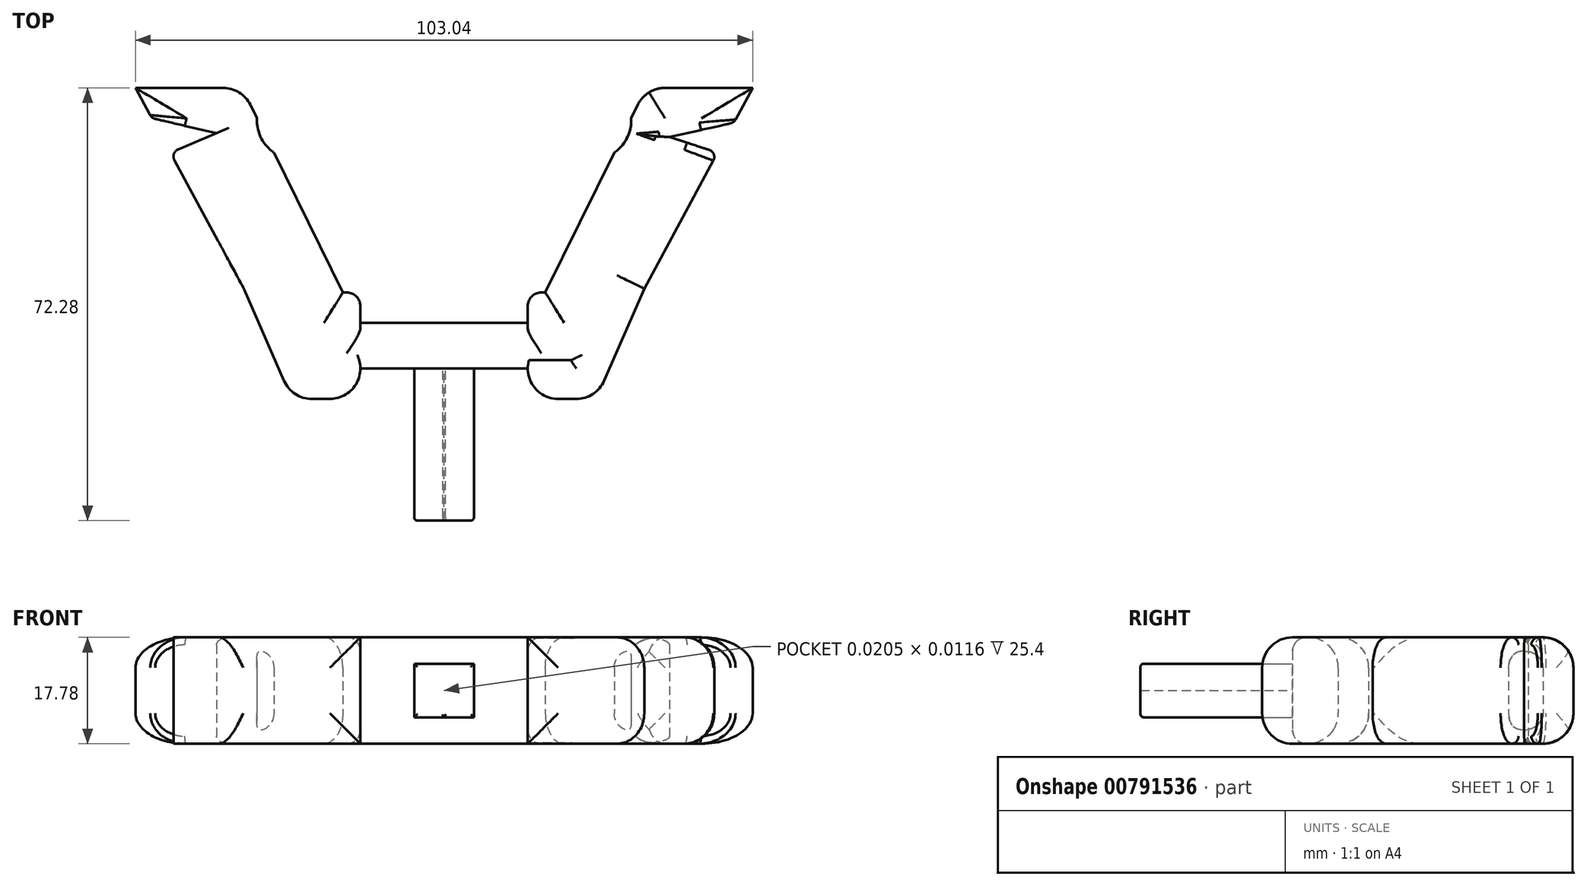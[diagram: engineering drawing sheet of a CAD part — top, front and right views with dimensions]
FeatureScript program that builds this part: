
annotation { "Feature Type Name" : "Feature", "Feature Type Description" : "" }
export const myFeature = defineFeature(function(context is Context, id is Id, definition is map)
    precondition{}
    {
        {
            var Q0;
            Q0=qCreatedBy(makeId("Top.planeOp"),FACE);
            var sketch = newSketch(context, id + "F0", { "sketchPlane" : qUnion([Q0])});
            skLineSegment(sketch, "E0", {"start": v(-38.82, 33.53) * mm, "end": v(-21.04, 33.53) * mm});
            skLineSegment(sketch, "E1", {"start": v(-38.82, 33.53) * mm, "end": v(-36.1, 28.48) * mm});
            skLineSegment(sketch, "E2", {"start": v(-21.04, 33.53) * mm, "end": v(-18.55, 28.48) * mm});
            skLineSegment(sketch, "E3", {"start": v(-4.2, -0.65) * mm, "end": v(-1.27, -0.65) * mm});
            skLineSegment(sketch, "E4", {"start": v(-20.73, 0) * mm, "end": v(-12.7, -18.43) * mm});
            skLineSegment(sketch, "E5", {"start": v(26.67, -0.65) * mm, "end": v(26.67, -5.73) * mm});
            skLineSegment(sketch, "E6", {"start": v(-12.7, -18.43) * mm, "end": v(-1.27, -18.43) * mm});
            skLineSegment(sketch, "E7", {"start": v(-16.66, 33.6) * mm, "end": v(-2.37, 4.57) * mm});
            skLineSegment(sketch, "E8", {"start": v(26.67, -18.43) * mm, "end": v(26.67, -13.35) * mm});
            skLineSegment(sketch, "E9.MirrorCS", {"start": v(42.06, 33.6) * mm, "end": v(27.77, 4.57) * mm});
            skLineSegment(sketch, "E10.MirrorCS", {"start": v(46.44, 33.53) * mm, "end": v(43.95, 28.48) * mm});
            skLineSegment(sketch, "E11.MirrorCS", {"start": v(29.6, -0.65) * mm, "end": v(26.67, -0.65) * mm});
            skLineSegment(sketch, "E12.MirrorCS", {"start": v(38.1, -18.43) * mm, "end": v(26.67, -18.43) * mm});
            skLineSegment(sketch, "E13.MirrorCS", {"start": v(46.13, 0) * mm, "end": v(38.1, -18.43) * mm});
            skLineSegment(sketch, "E14.MirrorCS", {"start": v(64.22, 33.53) * mm, "end": v(61.1, 27.74) * mm});
            skLineSegment(sketch, "E15.MirrorCS", {"start": v(64.22, 33.53) * mm, "end": v(46.44, 33.53) * mm});
            skLineSegment(sketch, "E16.trimOffspring", {"start": v(26.67, -5.73) * mm, "end": v(26.67, -0.65) * mm});
            skLineSegment(sketch, "E17.trimOffspring", {"start": v(26.67, -13.35) * mm, "end": v(26.67, -18.43) * mm});
            skLineSegment(sketch, "E18.trimOffspring", {"start": v(26.67, -5.73) * mm, "end": v(26.67, -1.8) * mm});
            skLineSegment(sketch, "E19", {"start": v(-1.27, -5.73) * mm, "end": v(-1.27, -0.65) * mm});
            skLineSegment(sketch, "E20", {"start": v(-1.27, -0.65) * mm, "end": v(-1.27, -5.73) * mm});
            skLineSegment(sketch, "E21.trimOffspring", {"start": v(-1.27, -13.35) * mm, "end": v(-1.27, -18.43) * mm});
            skArc(sketch, "E22", {"start": v(-18.55, 28.48) * mm, "mid": v(-17.88, 25.23) * mm, "end": v(-15.71, 22.72) * mm});
            skLineSegment(sketch, "E23.trimOffspring", {"start": v(-32.99, 22.72) * mm, "end": v(-20.73, 0) * mm});
            skLineSegment(sketch, "E24.trimOffspring", {"start": v(-15.71, 22.72) * mm, "end": v(-4.2, -0.65) * mm});
            skLineSegment(sketch, "E25", {"start": v(58.39, 22.72) * mm, "end": v(50.35, 25.32) * mm});
            skLineSegment(sketch, "E26", {"start": v(61.1, 27.74) * mm, "end": v(50.35, 25.32) * mm});
            skLineSegment(sketch, "E27.trimOffspring", {"start": v(58.39, 22.72) * mm, "end": v(46.13, 0) * mm});
            skLineSegment(sketch, "E28", {"start": v(-25.3, 25.97) * mm, "end": v(-36.1, 28.48) * mm});
            skLineSegment(sketch, "E29", {"start": v(-32.99, 22.72) * mm, "end": v(-25.3, 25.97) * mm});
            skLineSegment(sketch, "E30", {"start": v(-1.27, -5.73) * mm, "end": v(26.67, -5.73) * mm});
            skLineSegment(sketch, "E31", {"start": v(-1.27, -13.35) * mm, "end": v(26.67, -13.35) * mm});
            skArc(sketch, "E32", {"start": v(41.11, 22.72) * mm, "mid": v(43.28, 25.23) * mm, "end": v(43.95, 28.48) * mm});
            skLineSegment(sketch, "E33.trimOffspring", {"start": v(41.11, 22.72) * mm, "end": v(29.6, -0.65) * mm});
            skSolve(sketch);
        }
        {
            var Q0;
            Q0=makeQuery(id+"F0.imprint","IMPRINT",FACE,{"disambiguationData":[TD([[makeQuery(id+"F0.imprint","IMPRINT",EDGE,{"derivedFrom":sQuery(id+"F0.wireOp",EDGE,"E0")}),-1.0]])]});
            extrude(context, id + "F1", {"entities" : qUnion([Q0]), "depth" : 17.78 * mm, "offsetDistance" : 25.4 * mm});
        }
        {
            var Q0;
            Q0=makeQuery(id+"F1.opExtrude","CAP_EDGE",EDGE,{"disambiguationData":[OSD([sQuery(id+"F0.wireOp",EDGE,"E1")])],"isStart":false});
            var Q1;
            Q1=makeQuery(id+"F1.opExtrude","CAP_EDGE",EDGE,{"disambiguationData":[OSD([sQuery(id+"F0.wireOp",EDGE,"E2")])],"isStart":false});
            var Q2;
            Q2=makeQuery(id+"F1.opExtrude","CAP_EDGE",EDGE,{"disambiguationData":[OSD([sQuery(id+"F0.wireOp",EDGE,"E1")])],"isStart":true});
            var Q3;
            Q3=makeQuery(id+"F1.opExtrude","CAP_EDGE",EDGE,{"disambiguationData":[OSD([sQuery(id+"F0.wireOp",EDGE,"E2")])],"isStart":true});
            var Q4;
            Q4=makeQuery(id+"F1.opExtrude","SWEPT_FACE",FACE,{"disambiguationData":[OSD([sQuery(id+"F0.wireOp",EDGE,"E4")])]});
            var Q5;
            Q5=makeQuery(id+"F1.opExtrude","SWEPT_FACE",FACE,{"disambiguationData":[OSD([sQuery(id+"F0.wireOp",EDGE,"E6")])]});
            var Q6;
            Q6=makeQuery(id+"F1.opExtrude","CAP_EDGE",EDGE,{"disambiguationData":[OSD([sQuery(id+"F0.wireOp",EDGE,"E0")])],"isStart":false});
            var Q7;
            Q7=makeQuery(id+"F1.opExtrude","SWEPT_EDGE",EDGE,{"disambiguationData":[OSD([sQuery(id+"F0.wireOp",EDGE,"E0"),sQuery(id+"F0.wireOp",EDGE,"E2")])]});
            var Q8;
            Q8=makeQuery(id+"F1.opExtrude","CAP_EDGE",EDGE,{"disambiguationData":[OSD([sQuery(id+"F0.wireOp",EDGE,"E0")])],"isStart":true});
            fillet(context, id + "F2", {"entities" : qUnion([Q0, Q1, Q2, Q3, Q4, Q5, Q6, Q7, Q8]), "radius" : 5.08 * mm, "tangentPropagation" : true, "allowEdgeOverflow" : false});
        }
        {
            var Q0;
            Q0=makeQuery(id+"F1.opExtrude","CAP_EDGE",EDGE,{"disambiguationData":[OSD([sQuery(id+"F0.wireOp",EDGE,"E33.trimOffspring")])],"isStart":false});
            var Q1;
            Q1=makeQuery(id+"F1.opExtrude","CAP_EDGE",EDGE,{"disambiguationData":[OSD([sQuery(id+"F0.wireOp",EDGE,"E33.trimOffspring")])],"isStart":true});
            var Q2;
            Q2=makeQuery(id+"F1.opExtrude","CAP_EDGE",EDGE,{"disambiguationData":[OSD([sQuery(id+"F0.wireOp",EDGE,"E3")])],"isStart":false});
            var Q3;
            Q3=makeQuery(id+"F1.opExtrude","CAP_EDGE",EDGE,{"disambiguationData":[OSD([sQuery(id+"F0.wireOp",EDGE,"E3")])],"isStart":true});
            var Q4;
            Q4=makeQuery(id+"F1.opExtrude","CAP_EDGE",EDGE,{"disambiguationData":[OSD([sQuery(id+"F0.wireOp",EDGE,"E11.MirrorCS")])],"isStart":false});
            var Q5;
            Q5=makeQuery(id+"F1.opExtrude","CAP_EDGE",EDGE,{"disambiguationData":[OSD([sQuery(id+"F0.wireOp",EDGE,"E11.MirrorCS")])],"isStart":true});
            var Q6;
            Q6=makeQuery(id+"F1.opExtrude","CAP_EDGE",EDGE,{"disambiguationData":[OSD([sQuery(id+"F0.wireOp",EDGE,"E30")])],"isStart":true});
            var Q7;
            Q7=makeQuery(id+"F1.opExtrude","CAP_EDGE",EDGE,{"disambiguationData":[OSD([sQuery(id+"F0.wireOp",EDGE,"E30")])],"isStart":false});
            var Q8;
            Q8=makeQuery(id+"F1.opExtrude","CAP_EDGE",EDGE,{"disambiguationData":[OSD([sQuery(id+"F0.wireOp",EDGE,"E15.MirrorCS")])],"isStart":false});
            var Q9;
            Q9=makeQuery(id+"F1.opExtrude","CAP_EDGE",EDGE,{"disambiguationData":[OSD([sQuery(id+"F0.wireOp",EDGE,"E15.MirrorCS")])],"isStart":true});
            var Q10;
            Q10=makeQuery(id+"F1.opExtrude","CAP_EDGE",EDGE,{"disambiguationData":[OSD([sQuery(id+"F0.wireOp",EDGE,"E27.trimOffspring")])],"isStart":false});
            var Q11;
            Q11=makeQuery(id+"F1.opExtrude","CAP_EDGE",EDGE,{"disambiguationData":[OSD([sQuery(id+"F0.wireOp",EDGE,"E27.trimOffspring")])],"isStart":true});
            var Q12;
            Q12=makeQuery(id+"F1.opExtrude","SWEPT_EDGE",EDGE,{"disambiguationData":[OSD([sQuery(id+"F0.wireOp",EDGE,"E12.MirrorCS"),sQuery(id+"F0.wireOp",EDGE,"E13.MirrorCS")])]});
            var Q13;
            Q13=makeQuery(id+"F1.opExtrude","CAP_EDGE",EDGE,{"disambiguationData":[OSD([sQuery(id+"F0.wireOp",EDGE,"E12.MirrorCS")])],"isStart":true});
            var Q14;
            Q14=makeQuery(id+"F1.opExtrude","CAP_EDGE",EDGE,{"disambiguationData":[OSD([sQuery(id+"F0.wireOp",EDGE,"E12.MirrorCS")])],"isStart":false});
            var Q15;
            Q15=makeQuery(id+"F1.opExtrude","CAP_EDGE",EDGE,{"disambiguationData":[OSD([sQuery(id+"F0.wireOp",EDGE,"E14.MirrorCS")])],"isStart":false});
            var Q16;
            Q16=makeQuery(id+"F1.opExtrude","CAP_EDGE",EDGE,{"disambiguationData":[OSD([sQuery(id+"F0.wireOp",EDGE,"E14.MirrorCS")])],"isStart":true});
            var Q17;
            Q17=makeQuery(id+"F1.opExtrude","SWEPT_EDGE",EDGE,{"disambiguationData":[OSD([sQuery(id+"F0.wireOp",EDGE,"E10.MirrorCS"),sQuery(id+"F0.wireOp",EDGE,"E15.MirrorCS")])]});
            var Q18;
            Q18=makeQuery(id+"F1.opExtrude","SWEPT_EDGE",EDGE,{"disambiguationData":[OSD([sQuery(id+"F0.wireOp",EDGE,"E8"),sQuery(id+"F0.wireOp",EDGE,"E12.MirrorCS")])]});
            fillet(context, id + "F3", {"entities" : qUnion([Q0, Q1, Q2, Q3, Q4, Q5, Q6, Q7, Q8, Q9, Q10, Q11, Q12, Q13, Q14, Q15, Q16, Q17, Q18]), "radius" : 5.08 * mm, "tangentPropagation" : true, "allowEdgeOverflow" : false});
        }
        {
            var Q0;
            Q0=makeQuery(id+"F1.opExtrude","SWEPT_EDGE",EDGE,{"disambiguationData":[OSD([sQuery(id+"F0.wireOp",EDGE,"E5"),sQuery(id+"F0.wireOp",EDGE,"E11.MirrorCS")])]});
            var Q1;
            Q1=makeQuery(id+"F1.opExtrude","SWEPT_EDGE",EDGE,{"disambiguationData":[OSD([sQuery(id+"F0.wireOp",EDGE,"E3"),sQuery(id+"F0.wireOp",EDGE,"E19")])]});
            var Q2;
            Q2=makeQuery(id+"F1.opExtrude","CAP_EDGE",EDGE,{"disambiguationData":[OSD([sQuery(id+"F0.wireOp",EDGE,"E31")])],"isStart":true});
            var Q3;
            Q3=makeQuery(id+"F1.opExtrude","CAP_EDGE",EDGE,{"disambiguationData":[OSD([sQuery(id+"F0.wireOp",EDGE,"E31")])],"isStart":false});
            var Q4;
            Q4=makeQuery(id+"F3.opFillet","TWEAK_EDGE",EDGE,{"derivedFrom":[makeQuery(id+"F1.opExtrude","CAP_VERTEX",VERTEX,{"disambiguationData":[OSD([sQuery(id+"F0.wireOp",EDGE,"E5"),sQuery(id+"F0.wireOp",EDGE,"E30")])],"isStart":false})]});
            var Q5;
            Q5=makeQuery(id+"F3.opFillet","TWEAK_EDGE",EDGE,{"derivedFrom":[makeQuery(id+"F1.opExtrude","CAP_VERTEX",VERTEX,{"disambiguationData":[OSD([sQuery(id+"F0.wireOp",EDGE,"E5"),sQuery(id+"F0.wireOp",EDGE,"E30")])],"isStart":true})]});
            var Q6;
            Q6=makeQuery(id+"F3.opFillet","TWEAK_EDGE",EDGE,{"derivedFrom":[makeQuery(id+"F1.opExtrude","CAP_VERTEX",VERTEX,{"disambiguationData":[OSD([sQuery(id+"F0.wireOp",EDGE,"E19"),sQuery(id+"F0.wireOp",EDGE,"E30")])],"isStart":false})]});
            var Q7;
            Q7=makeQuery(id+"F3.opFillet","TWEAK_EDGE",EDGE,{"derivedFrom":[makeQuery(id+"F1.opExtrude","CAP_VERTEX",VERTEX,{"disambiguationData":[OSD([sQuery(id+"F0.wireOp",EDGE,"E19"),sQuery(id+"F0.wireOp",EDGE,"E30")])],"isStart":true})]});
            var Q8;
            Q8=makeQuery(id+"F3.opFillet","BLEND_EDGE",EDGE,{"blendedFrom":[makeQuery(id+"F1.opExtrude","CAP_EDGE",EDGE,{"disambiguationData":[OSD([sQuery(id+"F0.wireOp",EDGE,"E11.MirrorCS")])],"isStart":false}),makeQuery(id+"F1.opExtrude","SWEPT_FACE",FACE,{"disambiguationData":[OSD([sQuery(id+"F0.wireOp",EDGE,"E5")])]})],"blendedInto":[makeQuery(id+"F1.opExtrude","SWEPT_FACE",FACE,{"disambiguationData":[OSD([sQuery(id+"F0.wireOp",EDGE,"E5")])]})]});
            var Q9;
            Q9=makeQuery(id+"F3.opFillet","BLEND_EDGE",EDGE,{"blendedFrom":[makeQuery(id+"F1.opExtrude","CAP_EDGE",EDGE,{"disambiguationData":[OSD([sQuery(id+"F0.wireOp",EDGE,"E11.MirrorCS")])],"isStart":true}),makeQuery(id+"F1.opExtrude","SWEPT_FACE",FACE,{"disambiguationData":[OSD([sQuery(id+"F0.wireOp",EDGE,"E5")])]})],"blendedInto":[makeQuery(id+"F1.opExtrude","SWEPT_FACE",FACE,{"disambiguationData":[OSD([sQuery(id+"F0.wireOp",EDGE,"E5")])]})]});
            var Q10;
            Q10=makeQuery(id+"F3.opFillet","BLEND_EDGE",EDGE,{"blendedFrom":[makeQuery(id+"F1.opExtrude","CAP_EDGE",EDGE,{"disambiguationData":[OSD([sQuery(id+"F0.wireOp",EDGE,"E3")])],"isStart":true}),makeQuery(id+"F1.opExtrude","SWEPT_FACE",FACE,{"disambiguationData":[OSD([sQuery(id+"F0.wireOp",EDGE,"E19")])]})],"blendedInto":[makeQuery(id+"F1.opExtrude","SWEPT_FACE",FACE,{"disambiguationData":[OSD([sQuery(id+"F0.wireOp",EDGE,"E19")])]})]});
            var Q11;
            Q11=makeQuery(id+"F3.opFillet","BLEND_EDGE",EDGE,{"blendedFrom":[makeQuery(id+"F1.opExtrude","CAP_EDGE",EDGE,{"disambiguationData":[OSD([sQuery(id+"F0.wireOp",EDGE,"E3")])],"isStart":false}),makeQuery(id+"F1.opExtrude","SWEPT_FACE",FACE,{"disambiguationData":[OSD([sQuery(id+"F0.wireOp",EDGE,"E19")])]})],"blendedInto":[makeQuery(id+"F1.opExtrude","SWEPT_FACE",FACE,{"disambiguationData":[OSD([sQuery(id+"F0.wireOp",EDGE,"E19")])]})]});
            fillet(context, id + "F4", {"entities" : qUnion([Q0, Q1, Q2, Q3, Q4, Q5, Q6, Q7, Q8, Q9, Q10, Q11]), "radius" : 2.3 * mm, "tangentPropagation" : true, "allowEdgeOverflow" : false});
        }
        {
            var Q0;
            Q0=makeQuery(id+"F1.opExtrude","SWEPT_EDGE",EDGE,{"disambiguationData":[OSD([sQuery(id+"F0.wireOp",EDGE,"E25"),sQuery(id+"F0.wireOp",EDGE,"E27.trimOffspring")])]});
            var Q1;
            Q1=makeQuery(id+"F1.opExtrude","SWEPT_EDGE",EDGE,{"disambiguationData":[OSD([sQuery(id+"F0.wireOp",EDGE,"E14.MirrorCS"),sQuery(id+"F0.wireOp",EDGE,"E26")])]});
            var Q2;
            Q2=makeQuery(id+"F1.opExtrude","SWEPT_EDGE",EDGE,{"disambiguationData":[OSD([sQuery(id+"F0.wireOp",EDGE,"E1"),sQuery(id+"F0.wireOp",EDGE,"E28")])]});
            var Q3;
            Q3=makeQuery(id+"F1.opExtrude","SWEPT_EDGE",EDGE,{"disambiguationData":[OSD([sQuery(id+"F0.wireOp",EDGE,"E23.trimOffspring"),sQuery(id+"F0.wireOp",EDGE,"E29")])]});
            fillet(context, id + "F5", {"entities" : qUnion([Q0, Q1, Q2, Q3]), "radius" : 1.27 * mm, "tangentPropagation" : true, "allowEdgeOverflow" : false});
        }
        {
            var Q0;
            Q0=makeQuery(id+"F1.opExtrude","SWEPT_FACE",FACE,{"disambiguationData":[OSD([sQuery(id+"F0.wireOp",EDGE,"E31")])]});
            var sketch = newSketch(context, id + "F6", { "sketchPlane" : qUnion([Q0])});
            skLineSegment(sketch, "E34", {"start": v(26.67, 2.29) * mm, "end": v(-1.27, 2.29) * mm});
            skArc(sketch, "E35", {"start": v(12.48, 4.43) * mm, "mid": v(12.7, 4.42) * mm, "end": v(12.92, 4.43) * mm});
            skLineSegment(sketch, "E36", {"start": v(-1.27, 2.29) * mm, "end": v(26.67, 2.29) * mm});
            skLineSegment(sketch, "E37.bottom", {"start": v(8.23, 13.37) * mm, "end": v(17.17, 13.37) * mm});
            skLineSegment(sketch, "E37.top", {"start": v(8.23, 4.43) * mm, "end": v(17.17, 4.43) * mm});
            skLineSegment(sketch, "E38.bottom", {"start": v(17.17, 4.43) * mm, "end": v(8.23, 4.43) * mm});
            skLineSegment(sketch, "E38.top", {"start": v(17.17, 13.37) * mm, "end": v(8.23, 13.37) * mm});
            skLineSegment(sketch, "E39.trimOffspring", {"start": v(12.69, 8.88) * mm, "end": v(12.7, 8.9) * mm});
            skLineSegment(sketch, "E40.trimOffspring", {"start": v(12.7, 8.9) * mm, "end": v(12.7, 8.89) * mm});
            skPoint(sketch, "E41.trimOffspring.end.orphan", {"position": v(26.67, 15.5) * mm});
            skLineSegment(sketch, "E42", {"start": v(17.17, 13.37) * mm, "end": v(17.68, 13.37) * mm});
            skLineSegment(sketch, "E43", {"start": v(17.68, 13.37) * mm, "end": v(17.68, 4.43) * mm});
            skLineSegment(sketch, "E44", {"start": v(17.68, 4.43) * mm, "end": v(17.17, 4.43) * mm});
            skLineSegment(sketch, "E45", {"start": v(8.23, 4.43) * mm, "end": v(7.73, 4.43) * mm});
            skLineSegment(sketch, "E46", {"start": v(7.73, 4.43) * mm, "end": v(7.73, 13.37) * mm});
            skLineSegment(sketch, "E47", {"start": v(7.73, 13.37) * mm, "end": v(8.23, 13.37) * mm});
            skSolve(sketch);
        }
        {
            var Q0;
            Q0 = qSketchRegion(id + "F6", true);
            extrude(context, id + "F7", {"entities" : qUnion([Q0]), "operationType" : NewBodyOperationType.ADD, "depth" : 25.4 * mm, "offsetDistance" : 25.4 * mm});
        }
        {
            var Q0;
            Q0=makeQuery(id+"F7.opExtrude","CAP_EDGE",EDGE,{"disambiguationData":[OSD([sQuery(id+"F6.wireOp",EDGE,"E38.top"),sQuery(id+"F6.wireOp",EDGE,"E42"),sQuery(id+"F6.wireOp",EDGE,"E47")])],"isStart":false});
            var Q1;
            Q1=makeQuery(id+"F7.opExtrude","CAP_EDGE",EDGE,{"disambiguationData":[OSD([sQuery(id+"F6.wireOp",EDGE,"E38.bottom"),sQuery(id+"F6.wireOp",EDGE,"E44")])],"isStart":false});
            var Q2;
            Q2=makeQuery(id+"F7.opExtrude","CAP_EDGE",EDGE,{"disambiguationData":[OSD([sQuery(id+"F6.wireOp",EDGE,"E38.bottom"),sQuery(id+"F6.wireOp",EDGE,"E45")])],"isStart":false});
            var Q3;
            Q3=makeQuery(id+"F7.opExtrude","CAP_EDGE",EDGE,{"disambiguationData":[OSD([sQuery(id+"F6.wireOp",EDGE,"E35")])],"isStart":false});
            var Q4;
            Q4=makeQuery(id+"F7.opExtrude","CAP_EDGE",EDGE,{"disambiguationData":[OSD([sQuery(id+"F6.wireOp",EDGE,"E46")])],"isStart":false});
            var Q5;
            Q5=makeQuery(id+"F7.opExtrude","CAP_EDGE",EDGE,{"disambiguationData":[OSD([sQuery(id+"F6.wireOp",EDGE,"E43")])],"isStart":false});
            fillet(context, id + "F8", {"entities" : qUnion([Q0, Q1, Q2, Q3, Q4, Q5]), "radius" : 0.5 * mm, "tangentPropagation" : true, "allowEdgeOverflow" : false});
        }
    });
